# Revit family: Wall_Cabinets-Teknion-RHWMD_Wall_Cabinet_with_Microwave_Section-R2018
name_source: partatom
category: Furniture
revit_build: Autodesk Revit 2018 (Build: 20190510_1515(x64)
units: mm (PartAtom-declared; Revit-internal decimal feet)

## family parameters
Always vertical = Yes
Cut with Voids When Loaded = No
OmniClass Number = 23.40.20.00
OmniClass Title = General Furniture and Specialties
Room Calculation Point = No
Shared = Yes
Work Plane-Based = No

## types (5) — shared parameters
Assembly Code = E2020200
For Additional Finishes please visit = https://assets.teknion.com
Manufacturer = Teknion
Manufacturer Fax = 416.661.4586
Part Number = RHWMD
Product Documentation Link = https://www.teknion.com
Product Line = Modular Cabinets
Product Page URL = https://www.teknion.com
Series = Modular Cabinets
Sustainability Data = https://www.teknion.com
To render please download texture images found here = https://assets.teknion.com
URL = www.teknion.com
Unit Weight URL = http://www.teknion.com
Warranty = http://www.teknion.com

## per-type parameters (varying)
| type | Description | Double Door Swing Arc Radius | Model | Width |
| 36" Width | Wall Cabinet with Microwave Section, 15" Depth, 36" Width | 18 " | RHWMD1536__ | 36 " |
| 33" Width | Wall Cabinet with Microwave Section, 15" Depth, 33" Width | 16.5 " | RHWMD1533__ | 33 " |
| 30" Width | Wall Cabinet with Microwave Section, 15" Depth, 30" Width | 15 " | RHWMD1530__ | 30 " |
| 27" Width | Wall Cabinet with Microwave Section, 15" Depth, 27" Width | 13.5 " | RHWMD1527__ | 27 " |
| 24" Width | Wall Cabinet with Microwave Section, 15" Depth, 24" Width | 12 " | RHWMD1524__ | 24 " |

## geometry (parser evidence)
native form markers: Sweep x3
no freeform markers — native parametric forms only
